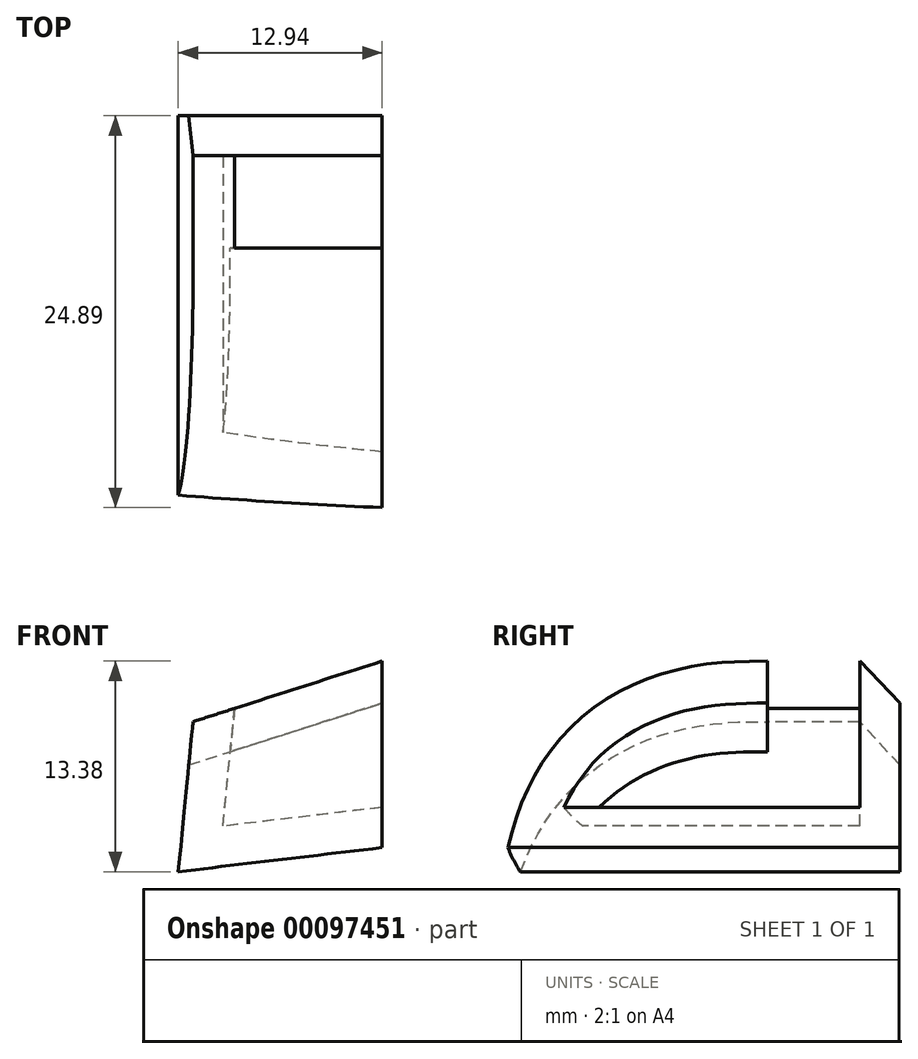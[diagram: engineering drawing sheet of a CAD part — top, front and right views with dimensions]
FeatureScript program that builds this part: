
annotation { "Feature Type Name" : "Feature", "Feature Type Description" : "" }
export const myFeature = defineFeature(function(context is Context, id is Id, definition is map)
    precondition{}
    {
        {
            var Q0;
            Q0=qCreatedBy(makeId("Front.planeOp"),FACE);
            var sketch = newSketch(context, id + "F0", { "sketchPlane" : qUnion([Q0])});
            skLineSegment(sketch, "E0", {"start": v(0.93, -12.42) * mm, "end": v(12.94, -8.57) * mm});
            skLineSegment(sketch, "E1", {"start": v(12.94, -8.57) * mm, "end": v(12.94, -20.42) * mm});
            skLineSegment(sketch, "E2", {"start": v(12.94, -20.42) * mm, "end": v(0, -21.95) * mm});
            skLineSegment(sketch, "E3", {"start": v(0, -21.95) * mm, "end": v(0.93, -12.42) * mm});
            skSolve(sketch);
        }
        {
            var Q0;
            Q0 = qSketchRegion(id + "F0", true);
            extrude(context, id + "F1", {"entities" : qUnion([Q0]), "oppositeDirection" : true, "depth" : 25.4 * mm});
        }
        {
            var Q0;
            Q0=makeQuery(id+"F1.opExtrude","CAP_EDGE",EDGE,{"disambiguationData":[OSD([sQuery(id+"F0.wireOp",EDGE,"E0")])],"isStart":true});
            fillet(context, id + "F2", {"entities" : qUnion([Q0]), "tangentPropagation" : true, "crossSection" : FilletCrossSection.CURVATURE, "radius" : 16.99 * mm, "magnitude" : 0.5, "defaultsChanged" : false, "vertexSettings" : []});
        }
        {
            var Q0;
            Q0=makeQuery(id+"F1.opExtrude","SWEPT_FACE",FACE,{"disambiguationData":[OSD([sQuery(id+"F0.wireOp",EDGE,"E1")])]});
            var Q1;
            Q1=makeQuery(id+"F1.opExtrude","SWEPT_FACE",FACE,{"disambiguationData":[OSD([sQuery(id+"F0.wireOp",EDGE,"E0")])]});
            shell(context, id + "F3", {"entities" : qUnion([Q0, Q1]), "thickness" : 2.54 * mm});
        }
        {
            var Q0;
            Q0=makeQuery(id+"F1.opExtrude","CAP_EDGE",EDGE,{"disambiguationData":[OSD([sQuery(id+"F0.wireOp",EDGE,"E0")])],"isStart":false});
            chamfer(context, id + "F4", {"entities" : qUnion([Q0]), "width" : 2.54 * mm, "tangentPropagation" : true});
        }
    });
